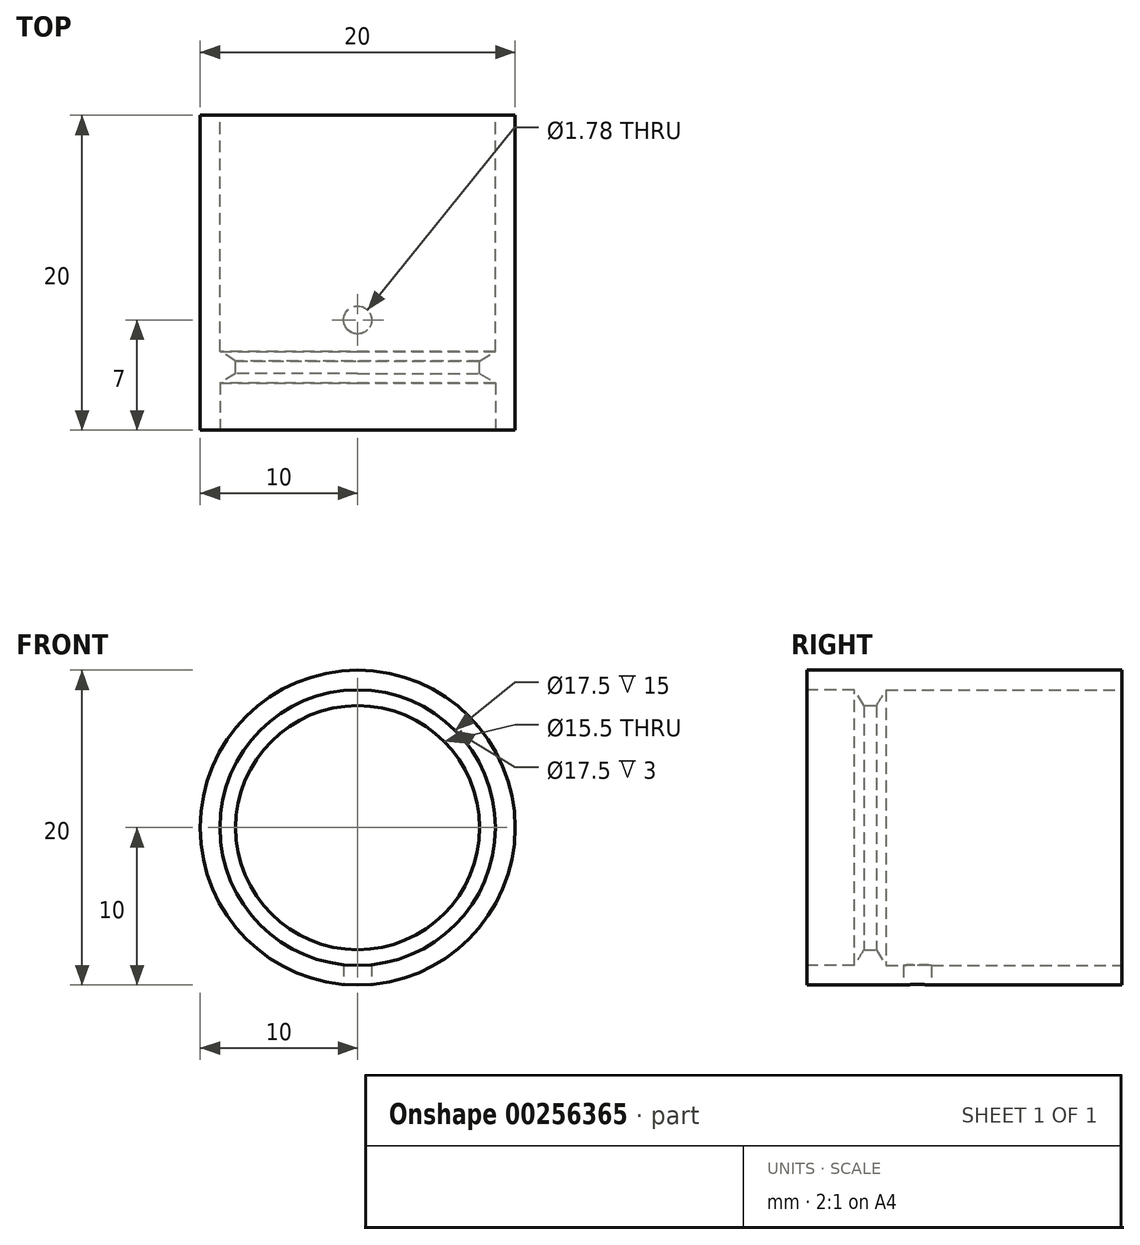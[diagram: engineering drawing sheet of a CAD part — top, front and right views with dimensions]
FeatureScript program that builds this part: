
annotation { "Feature Type Name" : "Feature", "Feature Type Description" : "" }
export const myFeature = defineFeature(function(context is Context, id is Id, definition is map)
    precondition{}
    {
        {
            var Q0;
            Q0=qCreatedBy(makeId("Front.planeOp"),FACE);
            var sketch = newSketch(context, id + "F0", { "sketchPlane" : qUnion([Q0])});
            skCircle(sketch, "E0", {"center": v(0, 0) * mm, "radius": 10 * mm});
            skSolve(sketch);
        }
        {
            var Q0;
            Q0=makeQuery(id+"F0.imprint","IMPRINT",FACE,{"disambiguationData":[TD([[makeQuery(id+"F0.imprint","IMPRINT",EDGE,{"derivedFrom":sQuery(id+"F0.wireOp",EDGE,"E0")}),1.0]])]});
            extrude(context, id + "F1", {"entities" : qUnion([Q0]), "depth" : 20 * mm});
        }
        {
            var Q0;
            Q0=makeQuery(id+"F1.opExtrude","CAP_FACE",FACE,{"disambiguationData":[OSD([sQuery(id+"F0.wireOp",EDGE,"E0")])],"isStart":true});
            var sketch = newSketch(context, id + "F2", { "sketchPlane" : qUnion([Q0])});
            skCircle(sketch, "E1", {"center": v(0, 0) * mm, "radius": 4.6 * mm});
            skSolve(sketch);
        }
        {
            var Q0;
            Q0=sQuery(id+"F2.wireOp",VERTEX,"E1.center");
            var Q1;
            Q1=makeQuery(id+"F1.opExtrude","SWEPT_BODY",BODY,{"disambiguationData":[OSD([sQuery(id+"F0.wireOp",EDGE,"E0")])]});
            hole(context, id + "F3", {"style" : HoleStyle.SIMPLE, "endStyle" : HoleEndStyle.THROUGH, "standardTappedOrClearance" : lookupTablePath({ "standard" : "ISO", "fit" : "Normal", "size" : "M14", "type" : "Clearance" }), "standardBlindInLast" : lookupTablePath({ "fit" : "Standard", "standard" : "ISO", "size" : "M14", "type" : "Clearance" }), "holeDiameter" : 15.5 * mm, "tappedDepth" : 12 * mm, "tapClearance" : 3, "locations" : qUnion([Q0]), "scope" : qUnion([Q1])});
        }
        {
            var Q0;
            Q0=makeQuery(id+"F1.opExtrude","CAP_FACE",FACE,{"disambiguationData":[OSD([sQuery(id+"F0.wireOp",EDGE,"E0")])],"isStart":false});
            var sketch = newSketch(context, id + "F4", { "sketchPlane" : qUnion([Q0])});
            skCircle(sketch, "E2", {"center": v(0, 0) * mm, "radius": 9.01 * mm});
            skSolve(sketch);
        }
        {
            var Q0;
            Q0=sQuery(id+"F4.wireOp",VERTEX,"E2.center");
            var Q1;
            Q1=makeQuery(id+"F1.opExtrude","SWEPT_BODY",BODY,{"disambiguationData":[OSD([sQuery(id+"F0.wireOp",EDGE,"E0")])]});
            hole(context, id + "F5", {"style" : HoleStyle.SIMPLE, "endStyle" : HoleEndStyle.BLIND, "standardTappedOrClearance" : lookupTablePath({ "standard" : "ISO", "fit" : "Normal", "size" : "M16", "type" : "Clearance" }), "standardBlindInLast" : lookupTablePath({ "fit" : "Standard", "standard" : "ISO", "size" : "M16", "type" : "Clearance" }), "holeDiameter" : 17.5 * mm, "holeDepth" : 3 * mm, "tappedDepth" : 12 * mm, "tapClearance" : 3, "locations" : qUnion([Q0]), "scope" : qUnion([Q1])});
        }
        {
            var Q0;
            Q0=makeQuery(id+"F1.opExtrude","CAP_FACE",FACE,{"disambiguationData":[OSD([sQuery(id+"F0.wireOp",EDGE,"E0")])],"isStart":true});
            var sketch = newSketch(context, id + "F6", { "sketchPlane" : qUnion([Q0])});
            skCircle(sketch, "E3", {"center": v(0, 0) * mm, "radius": 9.07 * mm});
            skSolve(sketch);
        }
        {
            var Q0;
            Q0=sQuery(id+"F6.wireOp",VERTEX,"E3.center");
            var Q1;
            Q1=makeQuery(id+"F1.opExtrude","SWEPT_BODY",BODY,{"disambiguationData":[OSD([sQuery(id+"F0.wireOp",EDGE,"E0")])]});
            hole(context, id + "F7", {"style" : HoleStyle.SIMPLE, "endStyle" : HoleEndStyle.BLIND, "standardTappedOrClearance" : lookupTablePath({ "standard" : "ISO", "fit" : "Normal", "size" : "M16", "type" : "Clearance" }), "standardBlindInLast" : lookupTablePath({ "fit" : "Standard", "standard" : "ISO", "size" : "M16", "type" : "Clearance" }), "holeDiameter" : 17.5 * mm, "holeDepth" : 15 * mm, "tappedDepth" : 12 * mm, "tapClearance" : 3, "locations" : qUnion([Q0]), "scope" : qUnion([Q1])});
        }
        {
            var Q0;
            Q0=qCreatedBy(makeId("Top.planeOp"),FACE);
            cPlane(context, id + "F8", {"entities" : qUnion([Q0]), "cplaneType" : CPlaneType.OFFSET, "offset" : 10 * mm, "oppositeDirection" : true, "width" : 150 * mm, "height" : 150 * mm});
        }
        {
            var Q0;
            Q0=qCreatedBy(id+"F8.planeOp",FACE);
            var sketch = newSketch(context, id + "F9", { "sketchPlane" : qUnion([Q0])});
            skPoint(sketch, "E4", {"position": v(0, -13) * mm});
            skSolve(sketch);
        }
        {
            var Q0;
            Q0=sQuery(id+"F9.wireOp",VERTEX,"E4");
            var Q1;
            Q1=makeQuery(id+"F1.opExtrude","SWEPT_BODY",BODY,{"disambiguationData":[OSD([sQuery(id+"F0.wireOp",EDGE,"E0")])]});
            hole(context, id + "F10", {"style" : HoleStyle.SIMPLE, "endStyle" : HoleEndStyle.BLIND, "oppositeDirection" : true, "standardTappedOrClearance" : lookupTablePath({ "standard" : "ANSI", "fit" : "Normal (ASME)", "size" : "#0", "type" : "Clearance" }), "standardBlindInLast" : lookupTablePath({ "fit" : "Free", "standard" : "ANSI", "size" : "#0", "type" : "Clearance" }), "holeDiameter" : 1.78 * mm, "holeDepth" : 12.95 * mm, "tappedDepth" : 12 * mm, "tapClearance" : 3, "locations" : qUnion([Q0]), "scope" : qUnion([Q1])});
        }
    });
